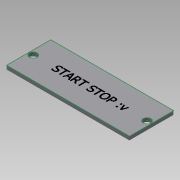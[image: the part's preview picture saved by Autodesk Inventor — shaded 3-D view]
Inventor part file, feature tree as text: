
AUTODESK INVENTOR PART (.ipt)
format: ipt  version: 2015 SP1 (Build 190203100, 203)  size: 85,504 bytes
history: native  units: mm
features: sketch x2, extrude x1, projected_geometry x1
ambient origin geometry x8: Origin, YZ Plane, XZ Plane, XY Plane, X Axis, Y Axis, Z Axis, Center Point
bodies: Solid1 (feature_tree)
feature tree (4):
  extrude  "Extrusion1"  Depth=19.939mm
  sketch  "Sketch2"  dims[d2=3.5mm d3=3.5mm d4=2.032mm d5=2.032mm d6=1.7mm d7=0.0mm]
  sketch  "Sketch1"  dims[d0=55.499mm d1=19.939mm]
  projected_geometry  "Projected Loop1"
